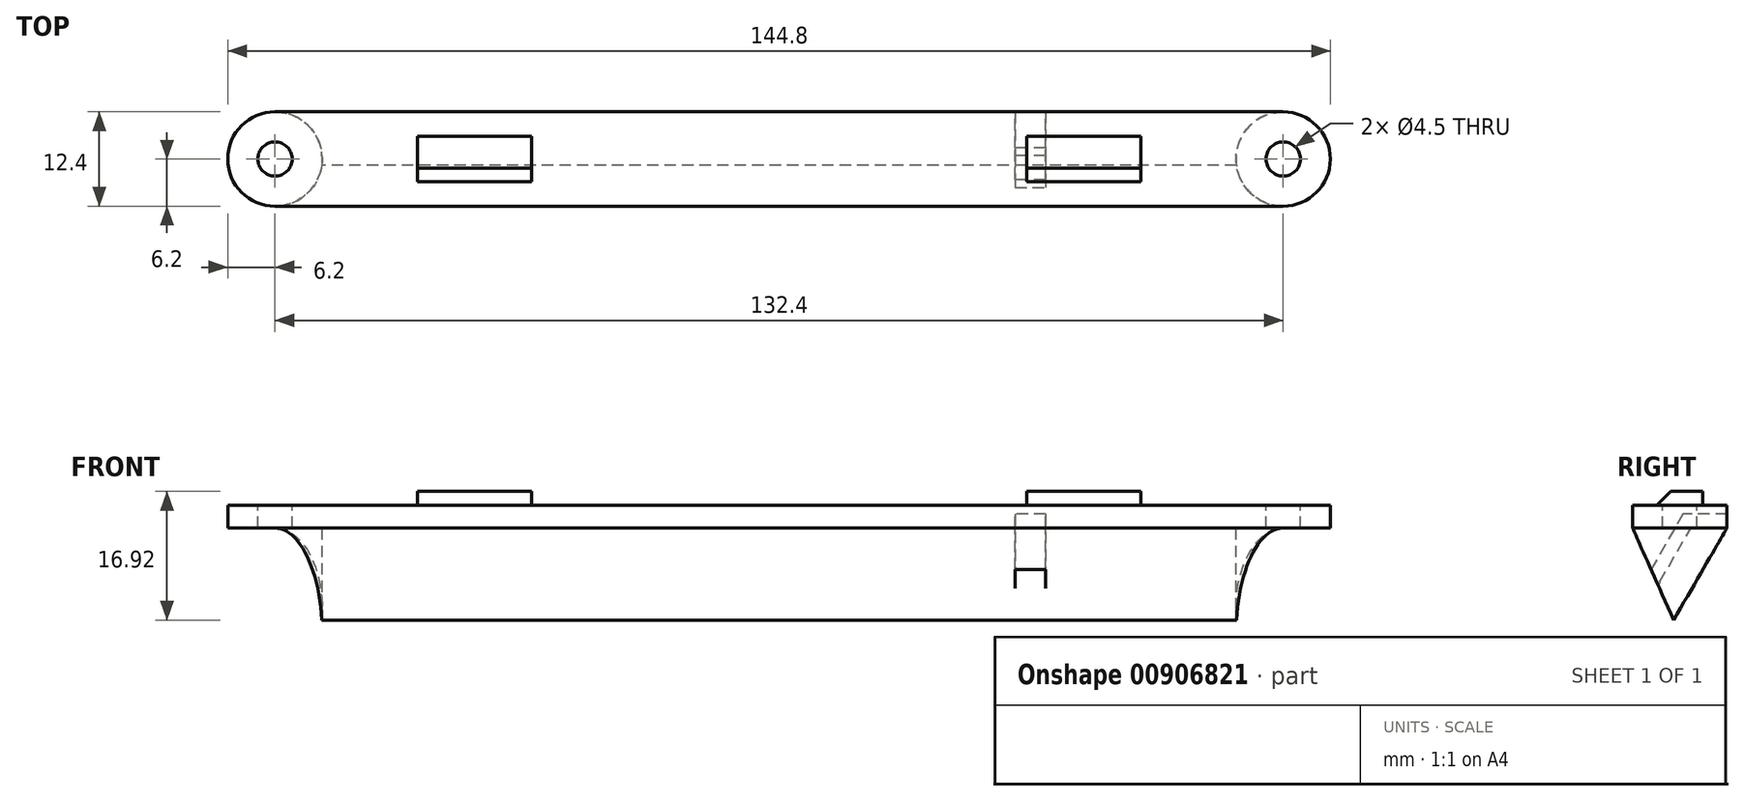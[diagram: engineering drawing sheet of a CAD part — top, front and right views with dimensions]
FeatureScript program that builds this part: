
annotation { "Feature Type Name" : "Feature", "Feature Type Description" : "" }
export const myFeature = defineFeature(function(context is Context, id is Id, definition is map)
    precondition{}
    {
        {
            var Q0;
            Q0=qCreatedBy(makeId("Top.planeOp"),FACE);
            var sketch = newSketch(context, id + "F0", { "sketchPlane" : qUnion([Q0])});
            skCircle(sketch, "E0", {"center": v(66.2, 0) * mm, "radius": 6.2 * mm});
            skCircle(sketch, "E1", {"center": v(-66.2, 0) * mm, "radius": 6.2 * mm});
            skLineSegment(sketch, "E2.bottom", {"start": v(-32.5, 3) * mm, "end": v(-47.5, 3) * mm});
            skLineSegment(sketch, "E2.top", {"start": v(-32.5, -3) * mm, "end": v(-47.5, -3) * mm});
            skLineSegment(sketch, "E2.left", {"start": v(-32.5, 3) * mm, "end": v(-32.5, -3) * mm});
            skLineSegment(sketch, "E2.right", {"start": v(-47.5, 3) * mm, "end": v(-47.5, -3) * mm});
            skPoint(sketch, "E2.middle", {"position": v(-40, 0) * mm});
            skLineSegment(sketch, "E3.bottom", {"start": v(47.5, 3) * mm, "end": v(32.5, 3) * mm});
            skLineSegment(sketch, "E3.top", {"start": v(47.5, -3) * mm, "end": v(32.5, -3) * mm});
            skLineSegment(sketch, "E3.left", {"start": v(47.5, 3) * mm, "end": v(47.5, -3) * mm});
            skLineSegment(sketch, "E3.right", {"start": v(32.5, 3) * mm, "end": v(32.5, -3) * mm});
            skPoint(sketch, "E3.middle", {"position": v(40, 0) * mm});
            skCircle(sketch, "E4", {"center": v(-66.2, 0) * mm, "radius": 2.25 * mm});
            skCircle(sketch, "E5", {"center": v(66.2, 0) * mm, "radius": 2.25 * mm});
            skLineSegment(sketch, "E6", {"start": v(-66.2, 6.2) * mm, "end": v(66.2, 6.2) * mm});
            skLineSegment(sketch, "E7", {"start": v(66.2, -6.2) * mm, "end": v(-66.2, -6.2) * mm});
            skSolve(sketch);
        }
        {
            var Q0;
            Q0=makeQuery(id+"F0.imprint","IMPRINT",FACE,{"disambiguationData":[TD([[makeQuery(id+"F0.imprint","IMPRINT",EDGE,{"derivedFrom":sQuery(id+"F0.wireOp",EDGE,"E2.bottom")}),1.0]])]});
            var Q1;
            Q1=makeQuery(id+"F0.imprint","IMPRINT",FACE,{"disambiguationData":[TD([[makeQuery(id+"F0.imprint","IMPRINT",EDGE,{"derivedFrom":sQuery(id+"F0.wireOp",EDGE,"E3.bottom")}),1.0]])]});
            var Q2;
            Q2=makeQuery(id+"F0.imprint","IMPRINT",FACE,{"disambiguationData":[TD([[makeQuery(id+"F0.imprint","IMPRINT",EDGE,{"derivedFrom":sQuery(id+"F0.wireOp",EDGE,"E2.bottom")}),-1.0]])]});
            extrude(context, id + "F1", {"entities" : qUnion([Q0, Q1, Q2]), "oppositeDirection" : true, "depth" : 30 * mm});
        }
        {
            var Q0;
            Q0=makeQuery(id+"F0.imprint","IMPRINT",FACE,{"disambiguationData":[TD([[makeQuery(id+"F0.imprint","IMPRINT",EDGE,{"derivedFrom":sQuery(id+"F0.wireOp",EDGE,"E2.bottom")}),1.0]])]});
            var Q1;
            Q1=makeQuery(id+"F0.imprint","IMPRINT",FACE,{"disambiguationData":[TD([[makeQuery(id+"F0.imprint","IMPRINT",EDGE,{"derivedFrom":sQuery(id+"F0.wireOp",EDGE,"E3.bottom")}),1.0]])]});
            extrude(context, id + "F2", {"entities" : qUnion([Q0, Q1]), "operationType" : NewBodyOperationType.ADD, "depth" : 1.8 * mm});
        }
        {
            var Q0;
            Q0=makeQuery(id+"F0.imprint","IMPRINT",FACE,{"disambiguationData":[TD([[makeQuery(id+"F0.imprint","IMPRINT",EDGE,{"derivedFrom":sQuery(id+"F0.wireOp",EDGE,"E4")}),-1.0]])]});
            var Q1;
            Q1=makeQuery(id+"F0.imprint","IMPRINT",FACE,{"disambiguationData":[TD([[makeQuery(id+"F0.imprint","IMPRINT",EDGE,{"derivedFrom":sQuery(id+"F0.wireOp",EDGE,"E5")}),-1.0]])]});
            extrude(context, id + "F3", {"entities" : qUnion([Q0, Q1]), "operationType" : NewBodyOperationType.ADD, "oppositeDirection" : true, "depth" : 3 * mm});
        }
        {
            var Q0;
            Q0=makeQuery(id+"F2.opExtrude","CAP_EDGE",EDGE,{"disambiguationData":[OSD([sQuery(id+"F0.wireOp",EDGE,"E3.top")])],"isStart":false});
            var Q1;
            Q1=makeQuery(id+"F2.opExtrude","CAP_EDGE",EDGE,{"disambiguationData":[OSD([sQuery(id+"F0.wireOp",EDGE,"E2.top")])],"isStart":false});
            chamfer(context, id + "F4", {"entities" : qUnion([Q0, Q1]), "width" : 1.8 * mm, "tangentPropagation" : true});
        }
        {
            var Q0;
            Q0=qCreatedBy(makeId("Right.planeOp"),FACE);
            var sketch = newSketch(context, id + "F5", { "sketchPlane" : qUnion([Q0])});
            skLineSegment(sketch, "E8", {"start": v(-6.2, -3) * mm, "end": v(6.2, -3) * mm});
            skLineSegment(sketch, "E9", {"start": v(6.2, -3) * mm, "end": v(-0.8, -15.12) * mm});
            skLineSegment(sketch, "E10", {"start": v(-0.8, -15.12) * mm, "end": v(-6.2, -3) * mm});
            skLineSegment(sketch, "E11", {"start": v(-6.2, -3) * mm, "end": v(-6.2, -30) * mm});
            skLineSegment(sketch, "E12", {"start": v(-6.2, -30) * mm, "end": v(6.2, -30) * mm});
            skLineSegment(sketch, "E13", {"start": v(6.2, -30) * mm, "end": v(6.2, -3) * mm});
            skSolve(sketch);
        }
        {
            var Q0;
            Q0=makeQuery(id+"F5.imprint","IMPRINT",FACE,{"disambiguationData":[TD([[makeQuery(id+"F5.imprint","IMPRINT",EDGE,{"derivedFrom":sQuery(id+"F5.wireOp",EDGE,"E9")}),1.0]])]});
            extrude(context, id + "F6", {"entities" : qUnion([Q0]), "operationType" : NewBodyOperationType.REMOVE, "endBound" : BoundingType.UP_TO_NEXT, "depth" : 120 * mm, "hasSecondDirection" : true, "secondDirectionBound" : BoundingType.UP_TO_NEXT, "secondDirectionOppositeDirection" : true, "secondDirectionDepth" : 25 * mm});
        }
        {
            var Q0;
            Q0=qCreatedBy(makeId("Right.planeOp"),FACE);
            var sketch = newSketch(context, id + "F7", { "sketchPlane" : qUnion([Q0])});
            skLineSegment(sketch, "E14", {"start": v(6.2, -1.2) * mm, "end": v(0.43, -1.2) * mm});
            skLineSegment(sketch, "E15", {"start": v(0.43, -1.2) * mm, "end": v(-6.2, -12.68) * mm});
            skLineSegment(sketch, "E16", {"start": v(-6.2, -12.68) * mm, "end": v(-6.2, -16.28) * mm});
            skLineSegment(sketch, "E17", {"start": v(-6.2, -16.28) * mm, "end": v(1.47, -3) * mm});
            skLineSegment(sketch, "E18", {"start": v(1.47, -3) * mm, "end": v(6.2, -3) * mm});
            skLineSegment(sketch, "E19", {"start": v(6.2, -3) * mm, "end": v(6.2, -1.2) * mm});
            skSolve(sketch);
        }
        {
            var Q0;
            Q0=makeQuery(id+"F7.imprint","IMPRINT",FACE,{"disambiguationData":[TD([[makeQuery(id+"F7.imprint","IMPRINT",EDGE,{"derivedFrom":sQuery(id+"F7.wireOp",EDGE,"E14")}),1.0]])]});
            extrude(context, id + "F8", {"entities" : qUnion([Q0]), "operationType" : NewBodyOperationType.REMOVE, "depth" : (33 + 2) * mm, "hasSecondDirection" : true, "secondDirectionOppositeDirection" : false, "secondDirectionDepth" : (33 - 2) * mm});
        }
        {
            var Q0;
            Q0=makeQuery(id+"F6.boolean.opBoolean","COPY",EDGE,{"derivedFrom":makeQuery(id+"F6.opExtrude","TWEAK_EDGE",EDGE,{"derivedFrom":[makeQuery(id+"F5.imprint","IMPRINT",EDGE,{"derivedFrom":sQuery(id+"F5.wireOp",EDGE,"E9")}),makeQuery(id+"F5.imprint","IMPRINT",EDGE,{"derivedFrom":sQuery(id+"F5.wireOp",EDGE,"E10")})]})});
            var Q1;
            Q1=makeQuery(id+"F6.boolean.opBoolean","COPY",EDGE,{"derivedFrom":makeQuery(id+"F6.opExtrude","TWEAK_EDGE",EDGE,{"derivedFrom":[makeQuery(id+"F1.opExtrude","SWEPT_FACE",FACE,{"disambiguationData":[OSD([sQuery(id+"F0.wireOp",EDGE,"E1")])]}),makeQuery(id+"F5.imprint","IMPRINT",EDGE,{"derivedFrom":sQuery(id+"F5.wireOp",EDGE,"E9")})]})});
            var Q2;
            Q2=makeQuery(id+"F6.boolean.opBoolean","COPY",EDGE,{"derivedFrom":makeQuery(id+"F6.opExtrude","TWEAK_EDGE",EDGE,{"derivedFrom":[makeQuery(id+"F1.opExtrude","SWEPT_FACE",FACE,{"disambiguationData":[OSD([sQuery(id+"F0.wireOp",EDGE,"E1")])]}),makeQuery(id+"F5.imprint","IMPRINT",EDGE,{"derivedFrom":sQuery(id+"F5.wireOp",EDGE,"E10")})]})});
            var Q3;
            Q3=makeQuery(id+"F6.boolean.opBoolean","COPY",EDGE,{"derivedFrom":makeQuery(id+"F6.opExtrude","TWEAK_EDGE",EDGE,{"derivedFrom":[makeQuery(id+"F1.opExtrude","SWEPT_FACE",FACE,{"disambiguationData":[OSD([sQuery(id+"F0.wireOp",EDGE,"E0")])]}),makeQuery(id+"F5.imprint","IMPRINT",EDGE,{"derivedFrom":sQuery(id+"F5.wireOp",EDGE,"E10")})]})});
            var Q4;
            Q4=makeQuery(id+"F6.boolean.opBoolean","COPY",EDGE,{"derivedFrom":makeQuery(id+"F6.opExtrude","TWEAK_EDGE",EDGE,{"derivedFrom":[makeQuery(id+"F1.opExtrude","SWEPT_FACE",FACE,{"disambiguationData":[OSD([sQuery(id+"F0.wireOp",EDGE,"E0")])]}),makeQuery(id+"F5.imprint","IMPRINT",EDGE,{"derivedFrom":sQuery(id+"F5.wireOp",EDGE,"E9")})]})});
            var Q5;
            Q5=makeQuery(id+"Fy0fjpXj2qNrPrX_1.1.F8.boolean.opBoolean","INTERSECT",EDGE,{"derivedFrom":[makeQuery(id+"F6.boolean.opBoolean","COPY",FACE,{"derivedFrom":makeQuery(id+"F6.opExtrude","SWEPT_FACE",FACE,{"disambiguationData":[OSD([sQuery(id+"F5.wireOp",EDGE,"E10")])]})}),makeQuery(id+"Fy0fjpXj2qNrPrX_1.1.F8.opExtrude","SWEPT_FACE",FACE,{"disambiguationData":[OSD([sQuery(id+"F7.wireOp",EDGE,"E17")])]})]});
            var Q6;
            Q6=makeQuery(id+"F8.boolean.opBoolean","INTERSECT",EDGE,{"derivedFrom":[makeQuery(id+"F6.boolean.opBoolean","COPY",FACE,{"derivedFrom":makeQuery(id+"F6.opExtrude","SWEPT_FACE",FACE,{"disambiguationData":[OSD([sQuery(id+"F5.wireOp",EDGE,"E10")])]})}),makeQuery(id+"F8.opExtrude","SWEPT_FACE",FACE,{"disambiguationData":[OSD([sQuery(id+"F7.wireOp",EDGE,"E17")])]})]});
            fillet(context, id + "F9", {"entities" : qUnion([Q0, Q1, Q2, Q3, Q4, Q5, Q6]), "radius" : 1 * mm, "tangentPropagation" : true, "allowEdgeOverflow" : false});
        }
    });
